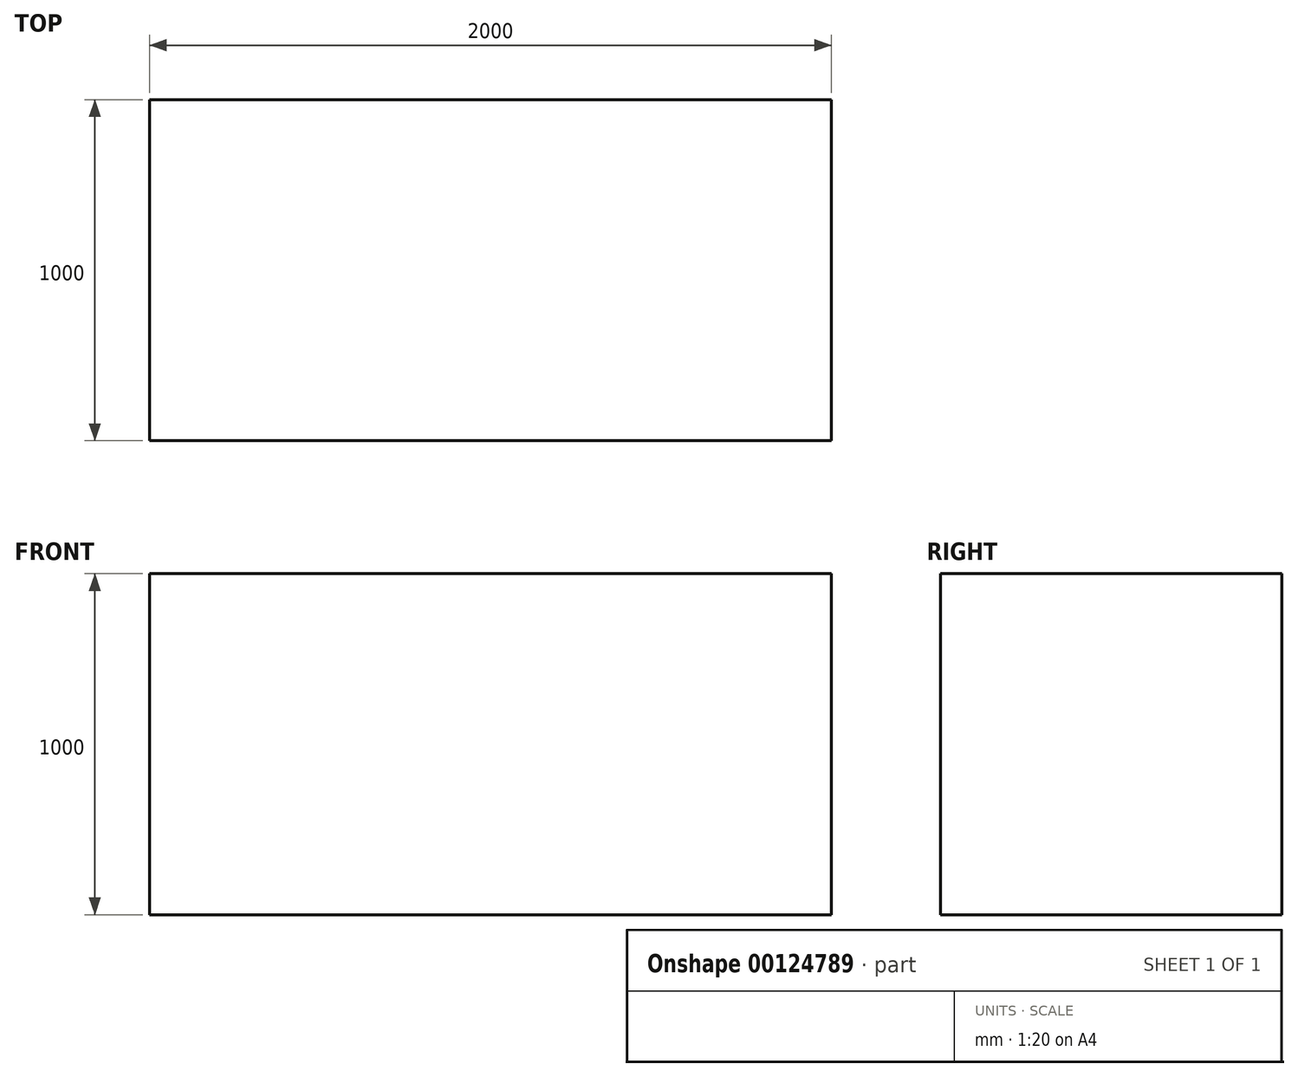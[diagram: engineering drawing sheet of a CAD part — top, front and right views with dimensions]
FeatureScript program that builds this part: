
annotation { "Feature Type Name" : "Feature", "Feature Type Description" : "" }
export const myFeature = defineFeature(function(context is Context, id is Id, definition is map)
    precondition{}
    {
        {
            var Q0;
            Q0=qCreatedBy(makeId("Front.planeOp"),FACE);
            var sketch = newSketch(context, id + "F0", { "sketchPlane" : qUnion([Q0])});
            skLineSegment(sketch, "E0.bottom", {"start": v(0, 0) * mm, "end": v(4000, 0) * mm});
            skLineSegment(sketch, "E0.top", {"start": v(0, 2000) * mm, "end": v(4000, 2000) * mm});
            skLineSegment(sketch, "E0.left", {"start": v(0, 0) * mm, "end": v(0, 2000) * mm});
            skLineSegment(sketch, "E0.right", {"start": v(4000, 0) * mm, "end": v(4000, 2000) * mm});
            skLineSegment(sketch, "E1.bottom", {"start": v(0, 0) * mm, "end": v(2000, 0) * mm});
            skLineSegment(sketch, "E1.top", {"start": v(0, 1000) * mm, "end": v(2000, 1000) * mm});
            skLineSegment(sketch, "E1.left", {"start": v(0, 0) * mm, "end": v(0, 1000) * mm});
            skLineSegment(sketch, "E1.right", {"start": v(2000, 0) * mm, "end": v(2000, 1000) * mm});
            skSolve(sketch);
        }
        {
            var Q0;
            Q0=makeQuery(id+"F0.imprint","IMPRINT",FACE,{"disambiguationData":[TD([[makeQuery(id+"F0.imprint","IMPRINT",EDGE,{"derivedFrom":sQuery(id+"F0.wireOp",EDGE,"E0.bottom")}),1.0]])]});
            extrude(context, id + "F1", {"entities" : qUnion([Q0]), "depth" : 1000 * mm});
        }
    });
